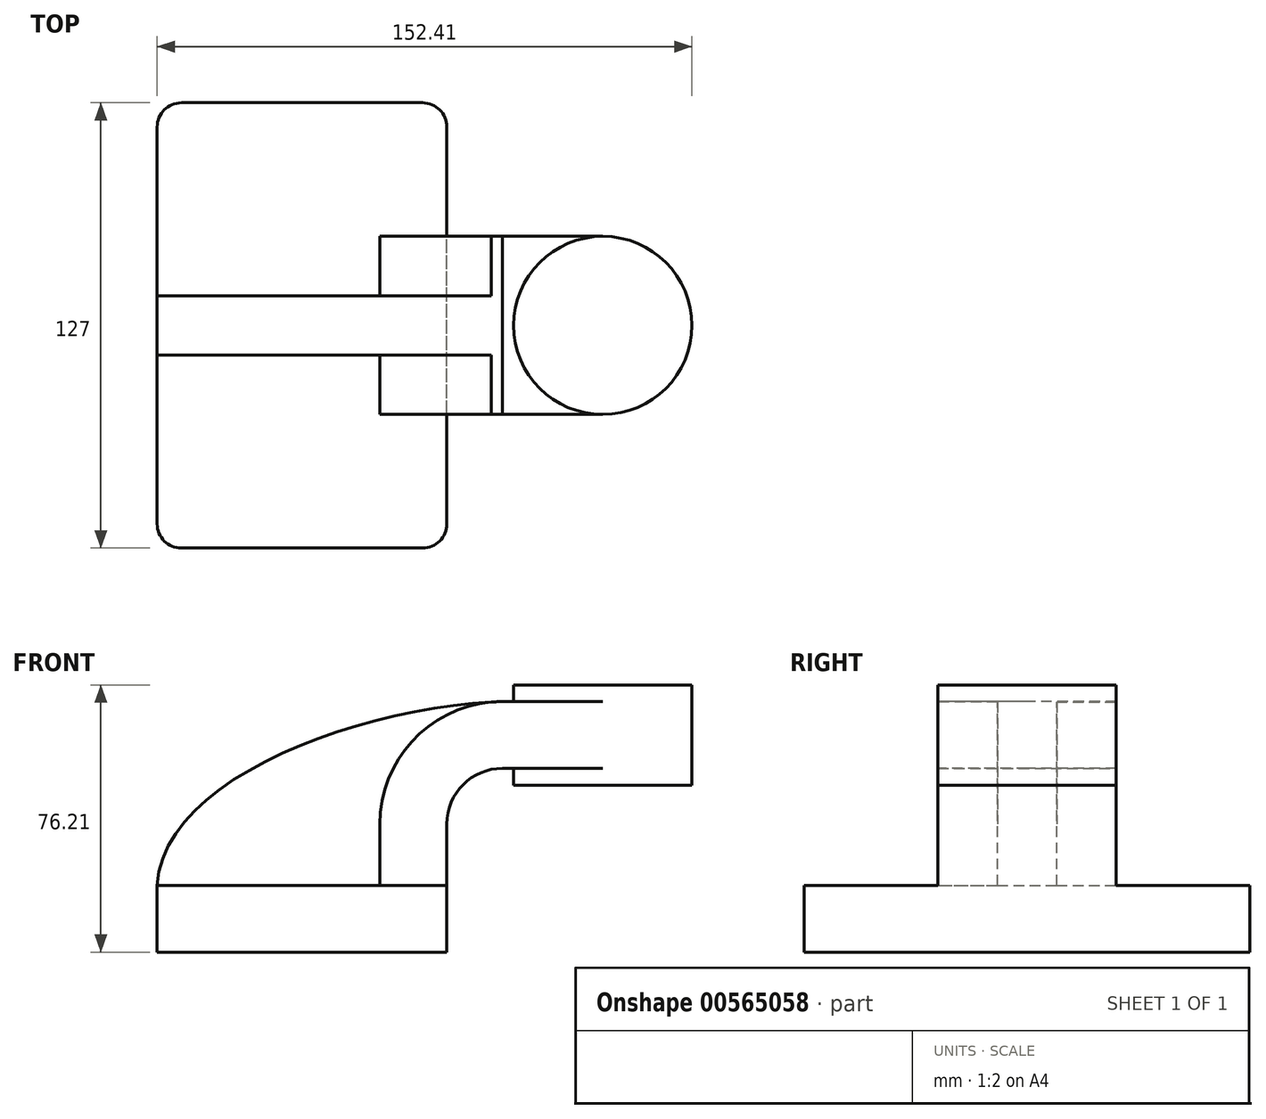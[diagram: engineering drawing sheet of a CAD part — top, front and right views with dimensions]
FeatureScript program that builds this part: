
annotation { "Feature Type Name" : "Feature", "Feature Type Description" : "" }
export const myFeature = defineFeature(function(context is Context, id is Id, definition is map)
    precondition{}
    {
        {
            var Q0;
            Q0=qCreatedBy(makeId("Front.planeOp"),FACE);
            var sketch = newSketch(context, id + "F0", { "sketchPlane" : qUnion([Q0])});
            skLineSegment(sketch, "E0.rect.bottom", {"start": v(-41.28, 9.52) * mm, "end": v(41.28, 9.52) * mm});
            skLineSegment(sketch, "E0.rect.top", {"start": v(-41.28, -9.52) * mm, "end": v(41.28, -9.52) * mm});
            skLineSegment(sketch, "E0.rect.left", {"start": v(-41.28, 9.52) * mm, "end": v(-41.28, -9.52) * mm});
            skLineSegment(sketch, "E0.rect.right", {"start": v(41.28, 9.52) * mm, "end": v(41.28, -9.52) * mm});
            skPoint(sketch, "E0.rect.middle", {"position": v(0, 0) * mm});
            skLineSegment(sketch, "E1", {"start": v(41.28, 9.52) * mm, "end": v(41.28, 27) * mm});
            skArc(sketch, "E2", {"start": v(41.28, 27) * mm, "mid": v(45.92, 38.23) * mm, "end": v(57.15, 42.88) * mm});
            skLineSegment(sketch, "E3", {"start": v(57.15, 42.88) * mm, "end": v(85.72, 42.88) * mm});
            skLineSegment(sketch, "E4.rect.bottom", {"start": v(60.32, 38.1) * mm, "end": v(111.12, 38.1) * mm});
            skLineSegment(sketch, "E4.rect.top", {"start": v(60.32, 66.68) * mm, "end": v(111.12, 66.68) * mm});
            skLineSegment(sketch, "E4.rect.left", {"start": v(60.32, 38.1) * mm, "end": v(60.32, 66.68) * mm});
            skLineSegment(sketch, "E4.rect.right", {"start": v(111.13, 38.1) * mm, "end": v(111.12, 66.68) * mm});
            skPoint(sketch, "E4.rect.middle", {"position": v(85.72, 52.39) * mm});
            skLineSegment(sketch, "E5.0", {"start": v(57.15, 61.93) * mm, "end": v(85.72, 61.93) * mm});
            skArc(sketch, "E5.1", {"start": v(22.23, 27) * mm, "mid": v(32.45, 51.7) * mm, "end": v(57.15, 61.93) * mm});
            skLineSegment(sketch, "E5.2", {"start": v(22.23, 9.52) * mm, "end": v(22.23, 27) * mm});
            skLineSegment(sketch, "E6", {"start": v(85.72, 38.1) * mm, "end": v(85.72, 66.68) * mm});
            skFitSpline(sketch, "E7", {"points": [v(-41.28, 9.53) * mm, v(57.15, 61.93) * mm], "startDerivative": vector(5.2, 92.34) * mm, "endDerivative": vector(120.92, 4.22) * mm});
            skSolve(sketch);
        }
        {
            var Q0;
            Q0=makeQuery(id+"F0.imprint","IMPRINT",FACE,{"disambiguationData":[TD([[makeQuery(id+"F0.imprint","IMPRINT",EDGE,{"derivedFrom":sQuery(id+"F0.wireOp",EDGE,"E0.rect.top")}),1.0]])]});
            extrude(context, id + "F1", {"entities" : qUnion([Q0]), "endBound" : BoundingType.SYMMETRIC, "depth" : 127 * mm});
        }
        {
            var Q0;
            {var subQ9=sQuery(id+"F0.wireOp",EDGE,"E1");Q0=makeQuery(id+"F0.imprint","IMPRINT",FACE,{"disambiguationData":[TD([[makeQuery(id+"F0.imprint","IMPRINT",EDGE,{"derivedFrom":subQ9}),1.0]])]});}
            var Q1;
            {var subQ0=sQuery(id+"F0.wireOp",EDGE,"E6");var subQ1=sQuery(id+"F0.wireOp",EDGE,"E3");var subQ2=makeQuery(id+"F0.imprint","INTERSECT",VERTEX,{"derivedFrom":[subQ1,subQ0]});Q1=makeQuery(id+"F0.imprint","IMPRINT",FACE,{"disambiguationData":[TD([[makeQuery(id+"F0.imprint","IMPRINT",EDGE,{"disambiguationData":[TD([[subQ2,1.0]])],"derivedFrom":subQ1}),1.0]])]});}
            extrude(context, id + "F2", {"entities" : qUnion([Q0, Q1]), "operationType" : NewBodyOperationType.ADD, "endBound" : BoundingType.SYMMETRIC, "depth" : 50.8 * mm});
        }
        {
            var Q0;
            {var subQ3=sQuery(id+"F0.wireOp",EDGE,"E5.2");Q0=makeQuery(id+"F0.imprint","IMPRINT",FACE,{"disambiguationData":[TD([[makeQuery(id+"F0.imprint","IMPRINT",EDGE,{"derivedFrom":subQ3}),1.0]])]});}
            extrude(context, id + "F3", {"entities" : qUnion([Q0]), "operationType" : NewBodyOperationType.ADD, "endBound" : BoundingType.SYMMETRIC, "depth" : 16.88 * mm, "offsetDistance" : 25 * mm});
        }
        {
            var Q0;
            {var subQ5=sQuery(id+"F0.wireOp",EDGE,"E4.rect.right");Q0=makeQuery(id+"F0.imprint","IMPRINT",FACE,{"disambiguationData":[TD([[makeQuery(id+"F0.imprint","IMPRINT",EDGE,{"derivedFrom":subQ5}),1.0]])]});}
            var Q1;
            Q1=sQuery(id+"F0.wireOp",EDGE,"E6");
            revolve(context, id + "F4", {"operationType" : NewBodyOperationType.ADD, "entities" : qUnion([Q0]), "axis" : qUnion([Q1]), "revolveType" : RevolveType.FULL});
        }
        {
            var Q0;
            Q0=makeQuery(id+"F1.opExtrude","CAP_EDGE",EDGE,{"disambiguationData":[OSD([sQuery(id+"F0.wireOp",EDGE,"E0.rect.right")])],"isStart":false});
            var Q1;
            Q1=makeQuery(id+"F1.opExtrude","CAP_EDGE",EDGE,{"disambiguationData":[OSD([sQuery(id+"F0.wireOp",EDGE,"E0.rect.left")])],"isStart":false});
            var Q2;
            Q2=makeQuery(id+"F1.opExtrude","CAP_EDGE",EDGE,{"disambiguationData":[OSD([sQuery(id+"F0.wireOp",EDGE,"E0.rect.right")])],"isStart":true});
            var Q3;
            Q3=makeQuery(id+"F1.opExtrude","CAP_EDGE",EDGE,{"disambiguationData":[OSD([sQuery(id+"F0.wireOp",EDGE,"E0.rect.left")])],"isStart":true});
            fillet(context, id + "F5", {"entities" : qUnion([Q0, Q1, Q2, Q3]), "radius" : 6.9 * mm, "tangentPropagation" : true, "allowEdgeOverflow" : false});
        }
    });
